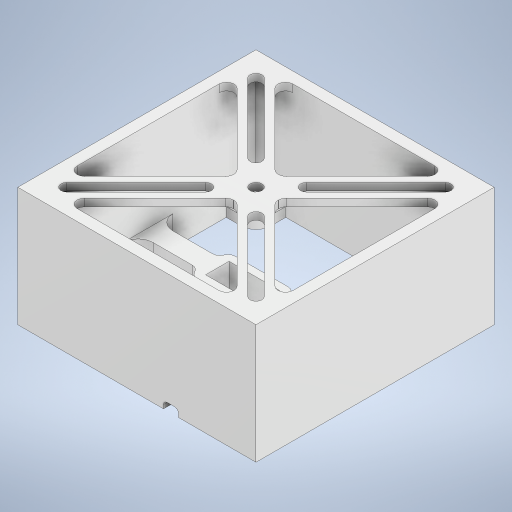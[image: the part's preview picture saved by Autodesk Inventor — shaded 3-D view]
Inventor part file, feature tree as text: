
AUTODESK INVENTOR PART (.ipt)
format: ipt  version: 2024 (Build 280153000, 153)  size: 527,360 bytes
history: native  units: in
note: dims shown in document units (in); Inventor stores cm internally (conversion verified against a paired STEP export)
features: fillet x9, extrude x6, sketch x6, pattern_circular x1, plane x1, projected_geometry x1
ambient origin geometry x8: Origin, YZ Plane, XZ Plane, XY Plane, X Axis, Y Axis, Z Axis, Center Point
bodies: Body1 (feature_tree)
feature tree (24):
  extrude  "Extrusion3"  Depth=4.0in
  extrude  "Extrusion4"  Depth=2.0in TaperAngle=0.0deg
  fillet  "Fillet2"  Radius=4.0in
  pattern_circular  "Circular Pattern1"  [2 undecoded]
  extrude  "Extrusion5"  Depth=0.125in
  fillet  "Fillet3"  Radius=1.5748in
  fillet  "Fillet4"  Radius=0.3346in
  fillet  "Fillet5"  Radius=0.7874in
  extrude  "Extrusion6"  Depth=0.125in
  fillet  "Fillet6"  Radius=0.5in
  fillet  "Fillet7"  Radius=0.0295in
  extrude  "Extrusion7"  Depth=0.125in
  fillet  "Fillet8"  Radius=0.125in
  extrude  "Extrusion8"  Depth=0.125in
  fillet  "Fillet9"  Radius=0.25in
  plane  "Work Plane1"
  fillet  "Fillet10"  Radius=0.5in
  sketch  "Sketch3"  dims[d17=4.0in d18=4.0in]
  sketch  "Sketch4"  dims[d19=0.1875in d20=2.0in d21=0.0in d22=4.0in]
  sketch  "Sketch5"  dims[d23=4.0in]
  sketch  "Sketch6"  dims[d24=0.1875in]
  projected_geometry  "Projected Loop1"
  sketch  "Sketch7"  dims[d25=0.25in]
  sketch  "Sketch8"  dims[d26=0.125in d27=0.1875in d28=0.0in d29=0.0312in d30=1.5748in d31=360.0deg d33=0.3346in d34=0.7874in d35=3.625in d36=0.5in d37=0.0in d38=0.0295in d39=0.125in d40=0.125in d41=0.125in d42=0.25in d43=0.5in d44=0.125in d45=0.0in d46=0.0312in d47=0.0312in d48=0.1875in d49=0.0in d50=0.0625in d51=0.75in d52=0.2in d53=3.625in d54=3.625in d55=0.2in d56=0.2in d58=0.125in d59=0.125in d60=1.5748in d62=360.0deg d64=0.125in d65=0.0in d66=0.125in d67=0.125in d16=0.0312in]
note: 2 required parameter values undecoded (feature->parameter linkage not recoverable at this tier; creation-order binding heuristic only, values carry confidence <= 0.55)
